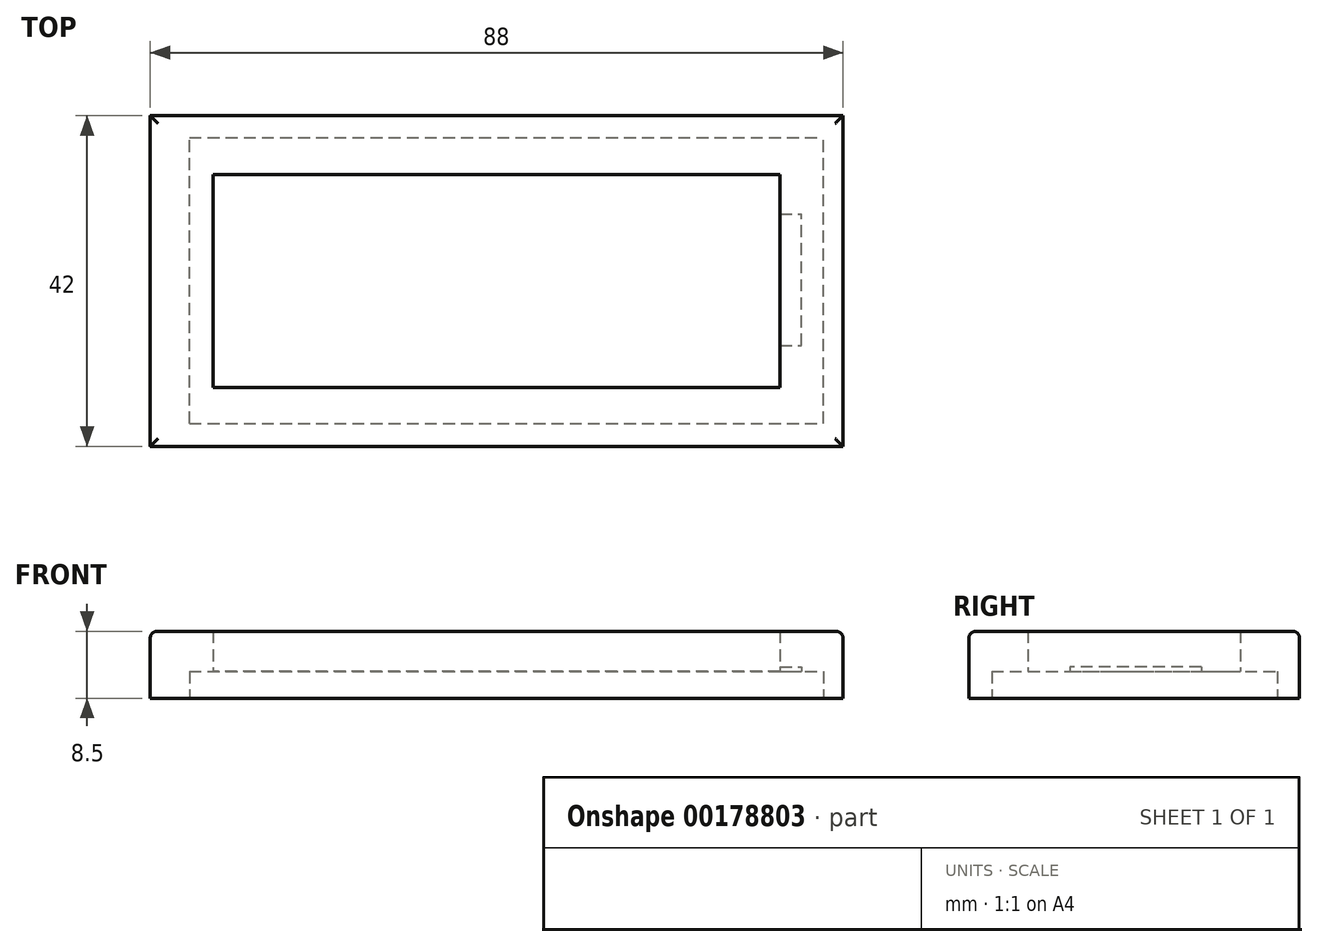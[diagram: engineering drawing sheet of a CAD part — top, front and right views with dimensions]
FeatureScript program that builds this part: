
annotation { "Feature Type Name" : "Feature", "Feature Type Description" : "" }
export const myFeature = defineFeature(function(context is Context, id is Id, definition is map)
    precondition{}
    {
        {
            var Q0;
            Q0=qCreatedBy(makeId("Top.planeOp"),FACE);
            var sketch = newSketch(context, id + "F0", { "sketchPlane" : qUnion([Q0])});
            skLineSegment(sketch, "E0", {"start": v(-44, 21) * mm, "end": v(44, 21) * mm});
            skLineSegment(sketch, "E1", {"start": v(44, 21) * mm, "end": v(44, -21) * mm});
            skLineSegment(sketch, "E2", {"start": v(44, -21) * mm, "end": v(-44, -21) * mm});
            skLineSegment(sketch, "E3", {"start": v(-44, -21) * mm, "end": v(-44, 21) * mm});
            skLineSegment(sketch, "E4.bottom", {"start": v(-36, 13.5) * mm, "end": v(36, 13.5) * mm});
            skLineSegment(sketch, "E4.top", {"start": v(-36, -13.5) * mm, "end": v(36, -13.5) * mm});
            skLineSegment(sketch, "E4.left", {"start": v(-36, 13.5) * mm, "end": v(-36, -13.5) * mm});
            skLineSegment(sketch, "E4.right", {"start": v(36, 13.5) * mm, "end": v(36, -13.5) * mm});
            skLineSegment(sketch, "E5", {"start": v(0, 21) * mm, "end": v(0, 13.5) * mm, "construction": true});
            skPoint(sketch, "E5.endSnap0", {"position": v(0, 13.5) * mm});
            skLineSegment(sketch, "E6", {"start": v(0, -13.5) * mm, "end": v(0, -21) * mm, "construction": true});
            skLineSegment(sketch, "E7", {"start": v(-44, 0) * mm, "end": v(-36, 0) * mm, "construction": true});
            skLineSegment(sketch, "E8", {"start": v(36, 0) * mm, "end": v(44, 0) * mm, "construction": true});
            skLineSegment(sketch, "E9", {"start": v(0, 0) * mm, "end": v(44, 0) * mm, "construction": true});
            skLineSegment(sketch, "E10", {"start": v(0, 0) * mm, "end": v(-44, 0) * mm, "construction": true});
            skLineSegment(sketch, "E11", {"start": v(0, 21) * mm, "end": v(0, -21) * mm, "construction": true});
            skSolve(sketch);
        }
        {
            var Q0;
            Q0=makeQuery(id+"F0.imprint","IMPRINT",FACE,{"disambiguationData":[TD([[makeQuery(id+"F0.imprint","IMPRINT",EDGE,{"derivedFrom":sQuery(id+"F0.wireOp",EDGE,"E0")}),-1.0]])]});
            extrude(context, id + "F1", {"entities" : qUnion([Q0]), "depth" : 8.5 * mm});
        }
        {
            var Q0;
            Q0=makeQuery(id+"F1.opExtrude","CAP_FACE",FACE,{"disambiguationData":[OSD([sQuery(id+"F0.wireOp",EDGE,"E0"),sQuery(id+"F0.wireOp",EDGE,"E1"),sQuery(id+"F0.wireOp",EDGE,"E2"),sQuery(id+"F0.wireOp",EDGE,"E3"),sQuery(id+"F0.wireOp",EDGE,"E4.bottom"),sQuery(id+"F0.wireOp",EDGE,"E4.top"),sQuery(id+"F0.wireOp",EDGE,"E4.left"),sQuery(id+"F0.wireOp",EDGE,"E4.right")])],"isStart":true});
            var sketch = newSketch(context, id + "F2", { "sketchPlane" : qUnion([Q0])});
            skLineSegment(sketch, "E12.bottom", {"start": v(36, 8.2) * mm, "end": v(38.75, 8.2) * mm});
            skLineSegment(sketch, "E12.top", {"start": v(36, -8.5) * mm, "end": v(38.75, -8.5) * mm});
            skLineSegment(sketch, "E12.left", {"start": v(36, 8.2) * mm, "end": v(36, -8.5) * mm});
            skLineSegment(sketch, "E12.right", {"start": v(38.75, 8.2) * mm, "end": v(38.75, -8.5) * mm});
            skLineSegment(sketch, "E13.left", {"start": v(38.75, 3.1) * mm, "end": v(38.75, -2.8) * mm});
            skLineSegment(sketch, "E14", {"start": v(38.75, 3.1) * mm, "end": v(41.5, 3.1) * mm});
            skLineSegment(sketch, "E15", {"start": v(41.5, 3.1) * mm, "end": v(41.5, -2.8) * mm});
            skLineSegment(sketch, "E16.bottom", {"start": v(-39, 18.1) * mm, "end": v(41.5, 18.1) * mm});
            skLineSegment(sketch, "E16.top", {"start": v(-39, -18.2) * mm, "end": v(41.5, -18.2) * mm});
            skLineSegment(sketch, "E16.left", {"start": v(-39, 18.1) * mm, "end": v(-39, -18.2) * mm});
            skLineSegment(sketch, "E16.right", {"start": v(41.5, 18.1) * mm, "end": v(41.5, -18.2) * mm});
            skLineSegment(sketch, "E17", {"start": v(38.75, -2.8) * mm, "end": v(41.5, -2.8) * mm});
            skSolve(sketch);
        }
        {
            var Q0;
            {var subQ1=sQuery(id+"F2.wireOp",EDGE,"E12.bottom");Q0=makeQuery(id+"F2.imprint","IMPRINT",FACE,{"disambiguationData":[TD([[makeQuery(id+"F2.imprint","IMPRINT",EDGE,{"derivedFrom":subQ1}),-1.0]])]});}
            extrude(context, id + "F3", {"entities" : qUnion([Q0]), "operationType" : NewBodyOperationType.REMOVE, "oppositeDirection" : true, "depth" : 4 * mm});
        }
        {
            var Q0;
            Q0 = qSketchRegion(id + "F2", true);
            extrude(context, id + "F4", {"entities" : qUnion([Q0]), "operationType" : NewBodyOperationType.REMOVE, "oppositeDirection" : true, "depth" : 3.4 * mm});
        }
        {
            var Q0;
            Q0=makeQuery(id+"F1.opExtrude","CAP_EDGE",EDGE,{"disambiguationData":[OSD([sQuery(id+"F0.wireOp",EDGE,"E2")])],"isStart":false});
            var Q1;
            Q1=makeQuery(id+"F1.opExtrude","CAP_EDGE",EDGE,{"disambiguationData":[OSD([sQuery(id+"F0.wireOp",EDGE,"E1")])],"isStart":false});
            var Q2;
            Q2=makeQuery(id+"F1.opExtrude","CAP_EDGE",EDGE,{"disambiguationData":[OSD([sQuery(id+"F0.wireOp",EDGE,"E3")])],"isStart":false});
            var Q3;
            Q3=makeQuery(id+"F1.opExtrude","CAP_EDGE",EDGE,{"disambiguationData":[OSD([sQuery(id+"F0.wireOp",EDGE,"E0")])],"isStart":false});
            fillet(context, id + "F5", {"entities" : qUnion([Q0, Q1, Q2, Q3]), "radius" : 1 * mm, "tangentPropagation" : true, "rho" : 0.5, "crossSection" : FilletCrossSection.CONIC, "allowEdgeOverflow" : false});
        }
    });
